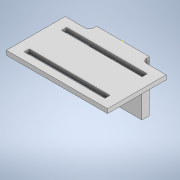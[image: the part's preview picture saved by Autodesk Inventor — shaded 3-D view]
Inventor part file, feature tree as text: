
AUTODESK INVENTOR PART (.ipt)
format: ipt  version: 2020 (Build 240168000, 168)  size: 399,360 bytes
history: native  units: in
note: dims shown in document units (in); Inventor stores cm internally (conversion verified against a paired STEP export)
features: extrude x10, sketch x10, fillet x2
ambient origin geometry x8: Origin, YZ Plane, XZ Plane, XY Plane, X Axis, Y Axis, Z Axis, Center Point
bodies: Solid1 (feature_tree)
feature tree (22):
  extrude  "Extrusion1"  Depth=1.2598in
  extrude  "Extrusion2"  Depth=0.1181in
  extrude  "Extrusion3"  Depth=1.5748in TaperAngle=360.0deg
  extrude  "Extrusion5"  Depth=0.1969in
  extrude  "Extrusion6"  Depth=0.0984in TaperAngle=0.0deg
  extrude  "Extrusion9"  Depth=0.3937in TaperAngle=0.0deg
  extrude  "Extrusion10"  Depth=0.1181in
  extrude  "Extrusion11"  Depth=1.7717in TaperAngle=0.0deg
  extrude  "Extrusion12"  Depth=0.6496in TaperAngle=0.0deg
  sketch  "Sketch15"  dims[d51=0.0787in d52=0.0in d53=0.6496in d54=0.0in]
  extrude  "Extrusion13"  Depth=2.1654in
  fillet  "Fillet2"  Radius=0.8661in
  fillet  "Fillet3"  Radius=0.1378in
  sketch  "Sketch1"  dims[d1=1.2598in d2=1.2598in]
  sketch  "Sketch2"  dims[d3=0.1969in d4=0.0in d5=0.1181in]
  sketch  "Sketch3"  dims[d6=0.374in d7=1.5748in d9=360.0deg]
  sketch  "Sketch5"  dims[d11=0.1969in d12=0.0in d13=0.2441in]
  sketch  "Sketch11"  dims[d14=1.5748in d16=360.0deg d18=0.0984in d19=0.0in]
  sketch  "Sketch12"  dims[d25=0.2362in d26=0.3937in d27=0.0in]
  sketch  "Sketch13"  dims[d32=1.2598in d33=0.1181in]
  sketch  "Sketch14"  dims[d34=1.7717in d35=0.0in d49=0.0787in d50=0.0in]
  sketch  "Sketch16"  dims[d55=0.6496in d56=0.0in d57=2.1654in d58=0.8661in d59=0.1378in d60=0.1378in d61=0.6496in d62=0.0in d63=0.1181in d64=0.1181in]
